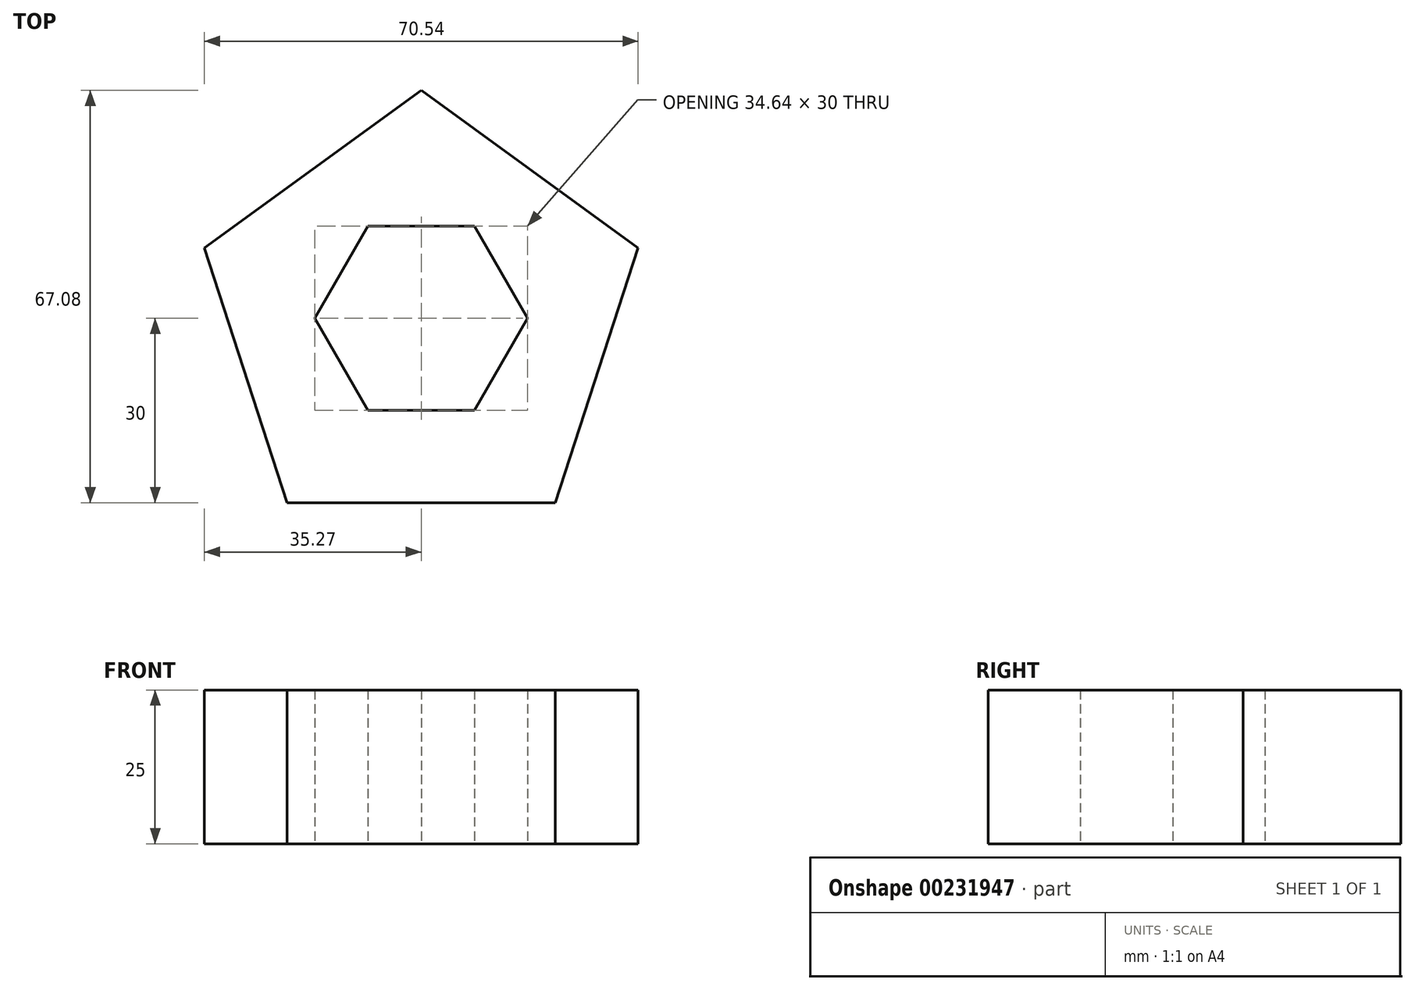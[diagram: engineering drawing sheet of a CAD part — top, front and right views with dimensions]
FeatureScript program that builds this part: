
annotation { "Feature Type Name" : "Feature", "Feature Type Description" : "" }
export const myFeature = defineFeature(function(context is Context, id is Id, definition is map)
    precondition{}
    {
        {
            var Q0;
            Q0=qCreatedBy(makeId("Top.planeOp"),FACE);
            var sketch = newSketch(context, id + "F0", { "sketchPlane" : qUnion([Q0])});
            skCircle(sketch, "E0.cCircle", {"center": v(0, 0) * mm, "radius": 15 * mm, "construction": true});
            skLineSegment(sketch, "E0.0", {"start": v(-8.66, 15) * mm, "end": v(8.66, 15) * mm});
            skLineSegment(sketch, "E0.1", {"start": v(8.66, 15) * mm, "end": v(17.32, 0) * mm});
            skLineSegment(sketch, "E0.2", {"start": v(17.32, 0) * mm, "end": v(8.66, -15) * mm});
            skLineSegment(sketch, "E0.3", {"start": v(8.66, -15) * mm, "end": v(-8.66, -15) * mm});
            skLineSegment(sketch, "E0.4", {"start": v(-8.66, -15) * mm, "end": v(-17.32, 0) * mm});
            skLineSegment(sketch, "E0.5", {"start": v(-17.32, 0) * mm, "end": v(-8.66, 15) * mm});
            skPoint(sketch, "E0.0.midPoint", {"position": v(0, 15) * mm});
            skCircle(sketch, "E1.cCircle", {"center": v(0, 0) * mm, "radius": 30 * mm, "construction": true});
            skLineSegment(sketch, "E1.0", {"start": v(35.27, 11.46) * mm, "end": v(21.8, -30) * mm});
            skLineSegment(sketch, "E1.1", {"start": v(21.8, -30) * mm, "end": v(-21.8, -30) * mm});
            skLineSegment(sketch, "E1.2", {"start": v(-21.8, -30) * mm, "end": v(-35.27, 11.46) * mm});
            skLineSegment(sketch, "E1.3", {"start": v(-35.27, 11.46) * mm, "end": v(0, 37.08) * mm});
            skLineSegment(sketch, "E1.4", {"start": v(0, 37.08) * mm, "end": v(35.27, 11.46) * mm});
            skPoint(sketch, "E1.0.midPoint", {"position": v(28.53, -9.27) * mm});
            skSolve(sketch);
        }
        {
            var Q0;
            Q0=makeQuery(id+"F0.imprint","IMPRINT",FACE,{"disambiguationData":[TD([[makeQuery(id+"F0.imprint","IMPRINT",EDGE,{"derivedFrom":sQuery(id+"F0.wireOp",EDGE,"E0.0")}),1.0]])]});
            extrude(context, id + "F1", {"entities" : qUnion([Q0]), "depth" : 25 * mm});
        }
    });
